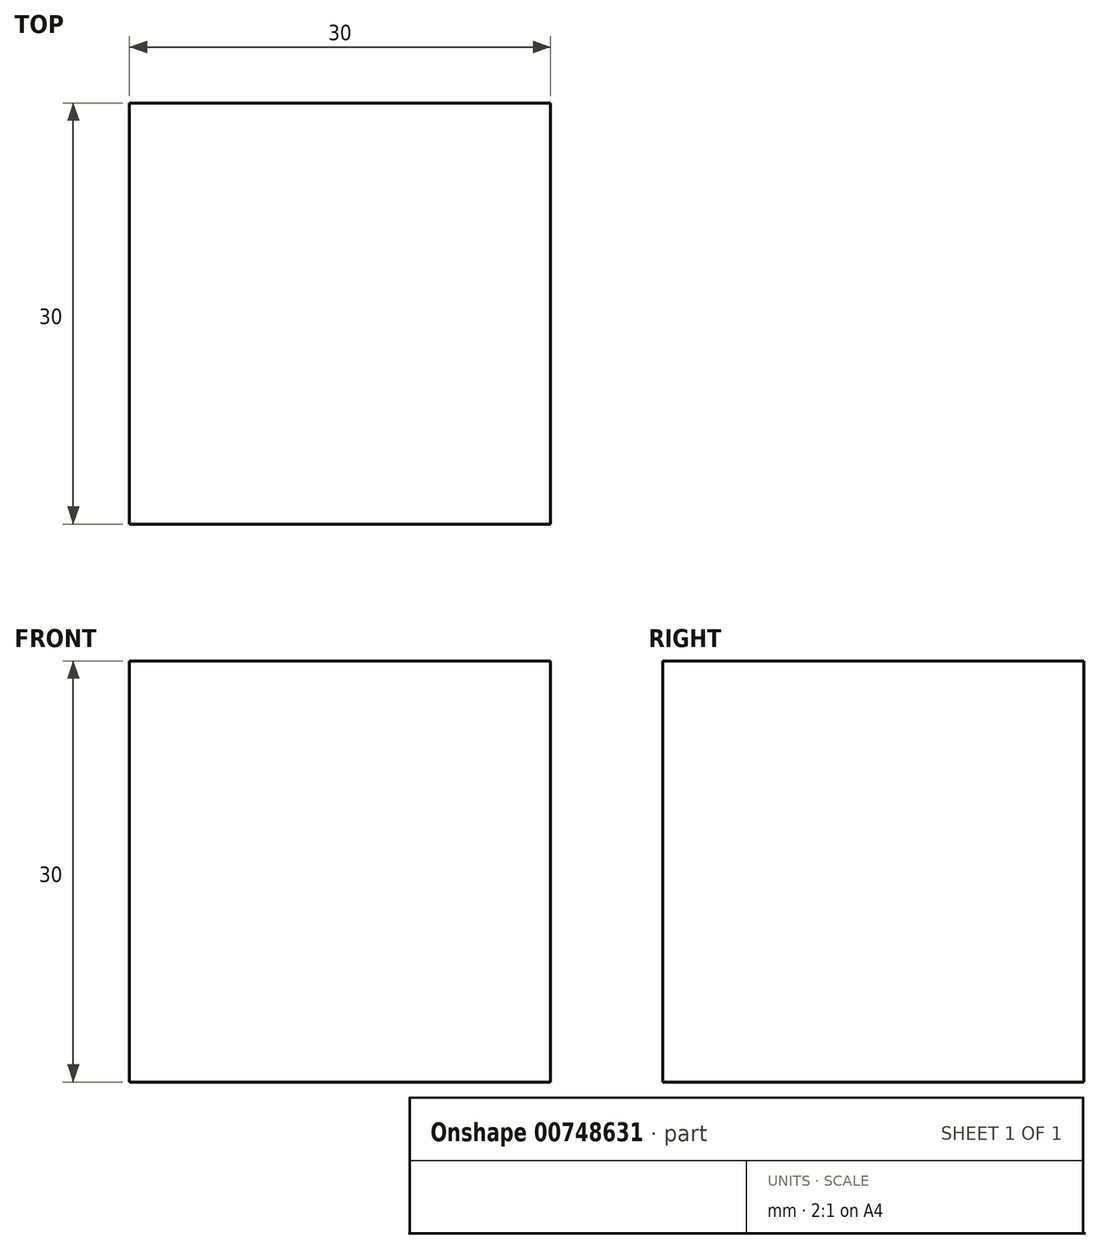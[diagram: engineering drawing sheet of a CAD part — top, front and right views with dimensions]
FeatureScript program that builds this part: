
annotation { "Feature Type Name" : "Feature", "Feature Type Description" : "" }
export const myFeature = defineFeature(function(context is Context, id is Id, definition is map)
    precondition{}
    {
        {
            var Q0;
            Q0=qCreatedBy(makeId("Top.planeOp"),FACE);
            var sketch = newSketch(context, id + "F0", { "sketchPlane" : qUnion([Q0])});
            skLineSegment(sketch, "E0.bottom", {"start": v(-22.3, 42.32) * mm, "end": v(7.7, 42.32) * mm});
            skLineSegment(sketch, "E0.top", {"start": v(-22.3, 12.32) * mm, "end": v(7.7, 12.32) * mm});
            skLineSegment(sketch, "E0.left", {"start": v(-22.3, 42.32) * mm, "end": v(-22.3, 12.32) * mm});
            skLineSegment(sketch, "E0.right", {"start": v(7.7, 42.32) * mm, "end": v(7.7, 12.32) * mm});
            skSolve(sketch);
        }
        {
            var Q0;
            Q0=makeQuery(id+"F0.imprint","IMPRINT",FACE,{"disambiguationData":[TD([[makeQuery(id+"F0.imprint","IMPRINT",EDGE,{"derivedFrom":sQuery(id+"F0.wireOp",EDGE,"E0.bottom")}),-1.0]])]});
            extrude(context, id + "F1", {"entities" : qUnion([Q0]), "depth" : 30 * mm, "offsetDistance" : 25 * mm});
        }
    });
